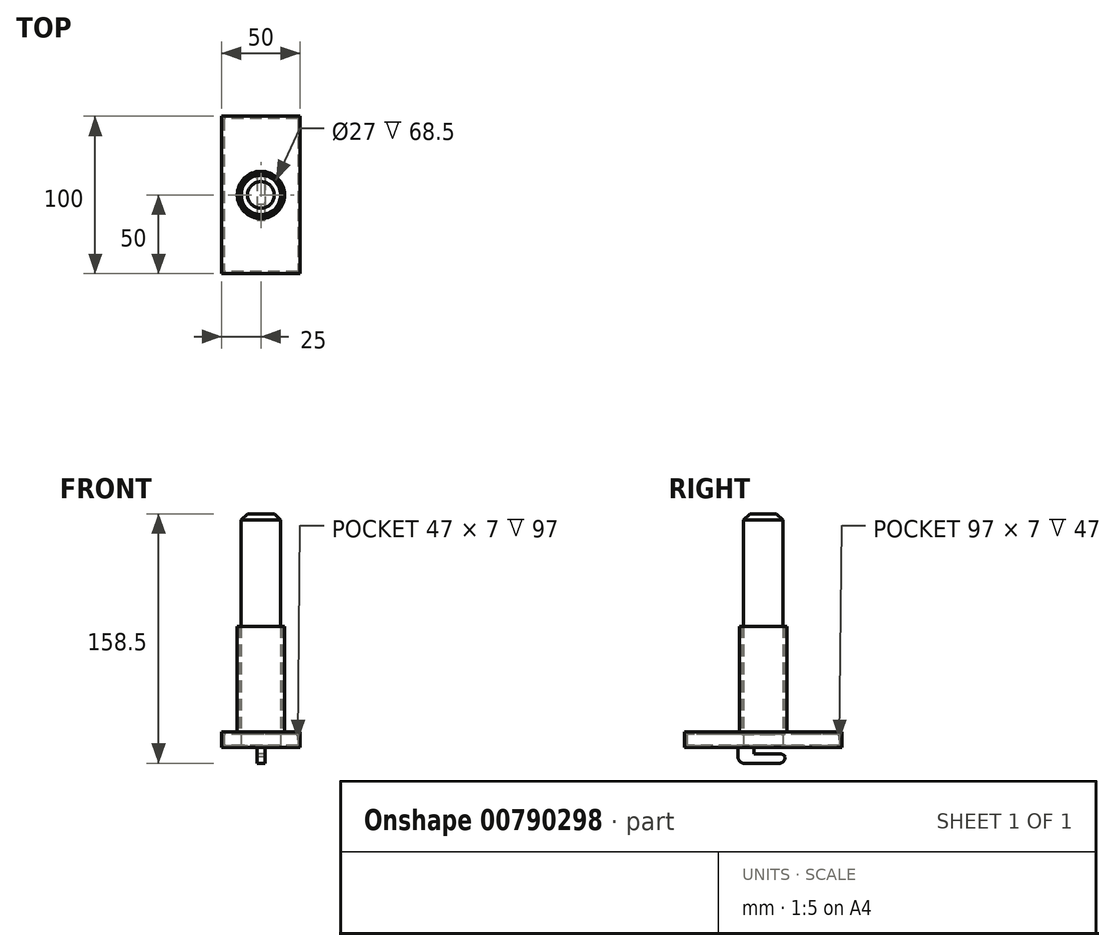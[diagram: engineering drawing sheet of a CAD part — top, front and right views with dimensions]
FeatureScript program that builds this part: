
annotation { "Feature Type Name" : "Feature", "Feature Type Description" : "" }
export const myFeature = defineFeature(function(context is Context, id is Id, definition is map)
    precondition{}
    {
        {
            var Q0;
            Q0=qCreatedBy(makeId("Top.planeOp"),FACE);
            var sketch = newSketch(context, id + "F0", { "sketchPlane" : qUnion([Q0])});
            skLineSegment(sketch, "E0.bottom", {"start": v(25, 50) * mm, "end": v(-25, 50) * mm});
            skLineSegment(sketch, "E0.top", {"start": v(25, -50) * mm, "end": v(-25, -50) * mm});
            skLineSegment(sketch, "E0.left", {"start": v(25, 50) * mm, "end": v(25, -50) * mm});
            skLineSegment(sketch, "E0.right", {"start": v(-25, 50) * mm, "end": v(-25, -50) * mm});
            skPoint(sketch, "E0.middle", {"position": v(0, 0) * mm});
            skSolve(sketch);
        }
        {
            var Q0;
            Q0 = qSketchRegion(id + "F0", true);
            extrude(context, id + "F1", {"entities" : qUnion([Q0]), "depth" : 10 * mm, "offsetDistance" : 25 * mm});
        }
        {
            var Q0;
            Q0=makeQuery(id+"F1.opExtrude","CAP_FACE",FACE,{"disambiguationData":[OSD([sQuery(id+"F0.wireOp",EDGE,"E0.bottom"),sQuery(id+"F0.wireOp",EDGE,"E0.top"),sQuery(id+"F0.wireOp",EDGE,"E0.left"),sQuery(id+"F0.wireOp",EDGE,"E0.right")])],"isStart":false});
            var sketch = newSketch(context, id + "F2", { "sketchPlane" : qUnion([Q0])});
            skCircle(sketch, "E1", {"center": v(0, 0) * mm, "radius": 15 * mm});
            skSolve(sketch);
        }
        {
            var Q0;
            Q0 = qSketchRegion(id + "F2", true);
            extrude(context, id + "F3", {"entities" : qUnion([Q0]), "operationType" : NewBodyOperationType.ADD, "depth" : 67 * mm, "offsetDistance" : 25 * mm});
        }
        {
            var Q0;
            Q0=makeQuery(id+"F3.opExtrude","CAP_FACE",FACE,{"disambiguationData":[OSD([sQuery(id+"F2.wireOp",EDGE,"E1")])],"isStart":false});
            shell(context, id + "F4", {"entities" : qUnion([Q0]), "thickness" : 1.5 * mm});
        }
        {
            var Q0;
            {var subQ0=sQuery(id+"F0.wireOp",EDGE,"E0.right");var subQ1=sQuery(id+"F0.wireOp",EDGE,"E0.left");var subQ2=sQuery(id+"F0.wireOp",EDGE,"E0.top");var subQ3=sQuery(id+"F0.wireOp",EDGE,"E0.bottom");Q0=makeQuery(id+"F4.opShell","OFFSET_FACE",FACE,{"disambiguationData":[OSD([subQ3,subQ2,subQ1,subQ0]),TDD([makeQuery(id+"F1.opExtrude","CAP_FACE",FACE,{"disambiguationData":[OSD([subQ3,subQ2,subQ1,subQ0])],"isStart":true})])]});}
            var sketch = newSketch(context, id + "F5", { "sketchPlane" : qUnion([Q0])});
            skCircle(sketch, "E2", {"center": v(0, 0) * mm, "radius": 12.5 * mm});
            skSolve(sketch);
        }
        {
            var Q0;
            Q0 = qSketchRegion(id + "F5", true);
            extrude(context, id + "F6", {"entities" : qUnion([Q0]), "operationType" : NewBodyOperationType.ADD, "depth" : 147 * mm, "offsetDistance" : 25 * mm});
        }
        {
            var Q0;
            Q0=makeQuery(id+"F6.opExtrude","CAP_EDGE",EDGE,{"disambiguationData":[OSD([sQuery(id+"F5.wireOp",EDGE,"E2")])],"isStart":false});
            chamfer(context, id + "F7", {"entities" : qUnion([Q0]), "width" : 4 * mm, "tangentPropagation" : true});
        }
        {
            var Q0;
            Q0=makeQuery(id+"F1.opExtrude","CAP_FACE",FACE,{"disambiguationData":[OSD([sQuery(id+"F0.wireOp",EDGE,"E0.bottom"),sQuery(id+"F0.wireOp",EDGE,"E0.top"),sQuery(id+"F0.wireOp",EDGE,"E0.left"),sQuery(id+"F0.wireOp",EDGE,"E0.right")])],"isStart":true});
            var sketch = newSketch(context, id + "F8", { "sketchPlane" : qUnion([Q0])});
            skLineSegment(sketch, "E3", {"start": v(0, 16) * mm, "end": v(-2.5, 16) * mm});
            skLineSegment(sketch, "E4", {"start": v(0, 16) * mm, "end": v(2.5, 16) * mm});
            skLineSegment(sketch, "E5", {"start": v(2.5, 16) * mm, "end": v(2.5, 6) * mm});
            skLineSegment(sketch, "E6", {"start": v(2.5, 6) * mm, "end": v(-2.5, 6) * mm});
            skLineSegment(sketch, "E7", {"start": v(-2.5, 6) * mm, "end": v(-2.5, 16) * mm});
            skSolve(sketch);
        }
        {
            var Q0;
            Q0 = qSketchRegion(id + "F8", true);
            extrude(context, id + "F9", {"entities" : qUnion([Q0]), "operationType" : NewBodyOperationType.ADD, "depth" : 10 * mm, "offsetDistance" : 25 * mm});
        }
        {
            var Q0;
            Q0=makeQuery(id+"F9.opExtrude","SWEPT_FACE",FACE,{"disambiguationData":[OSD([sQuery(id+"F8.wireOp",EDGE,"E6")])]});
            var sketch = newSketch(context, id + "F10", { "sketchPlane" : qUnion([Q0])});
            skLineSegment(sketch, "E8", {"start": v(2.5, -10) * mm, "end": v(-2.5, -10) * mm});
            skLineSegment(sketch, "E9", {"start": v(-2.5, -10) * mm, "end": v(-2.5, -4) * mm});
            skLineSegment(sketch, "E10", {"start": v(-2.5, -4) * mm, "end": v(2.5, -4) * mm});
            skLineSegment(sketch, "E11", {"start": v(2.5, -4) * mm, "end": v(2.5, -10) * mm});
            skSolve(sketch);
        }
        {
            var Q0;
            Q0 = qSketchRegion(id + "F10", true);
            extrude(context, id + "F11", {"entities" : qUnion([Q0]), "operationType" : NewBodyOperationType.ADD, "depth" : 20 * mm, "offsetDistance" : 25 * mm});
        }
        {
            var Q0;
            Q0=makeQuery(id+"F11.opExtrude","CAP_EDGE",EDGE,{"disambiguationData":[OSD([sQuery(id+"F10.wireOp",EDGE,"E8")])],"isStart":false});
            fillet(context, id + "F12", {"entities" : qUnion([Q0]), "radius" : 4 * mm, "tangentPropagation" : true, "allowEdgeOverflow" : false});
        }
        {
            var Q0;
            Q0=makeQuery(id+"F9.opExtrude","CAP_EDGE",EDGE,{"disambiguationData":[OSD([sQuery(id+"F8.wireOp",EDGE,"E3"),sQuery(id+"F8.wireOp",EDGE,"E4")])],"isStart":false});
            fillet(context, id + "F13", {"entities" : qUnion([Q0]), "radius" : 4 * mm, "tangentPropagation" : true, "allowEdgeOverflow" : false});
        }
        {
            var Q0;
            Q0=makeQuery(id+"F11.opExtrude","CAP_EDGE",EDGE,{"disambiguationData":[OSD([sQuery(id+"F10.wireOp",EDGE,"E10")])],"isStart":false});
            fillet(context, id + "F14", {"entities" : qUnion([Q0]), "radius" : 4 * mm, "tangentPropagation" : true, "allowEdgeOverflow" : false});
        }
    });
